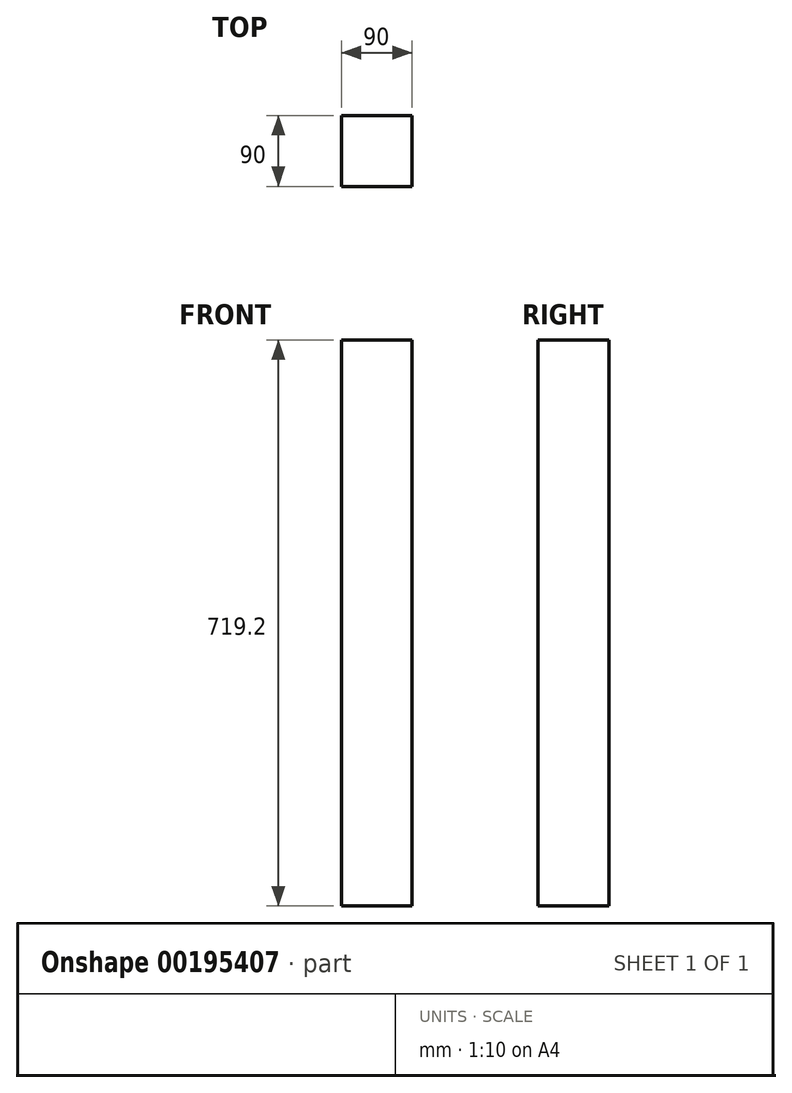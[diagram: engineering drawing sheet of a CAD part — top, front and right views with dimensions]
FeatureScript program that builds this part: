
annotation { "Feature Type Name" : "Feature", "Feature Type Description" : "" }
export const myFeature = defineFeature(function(context is Context, id is Id, definition is map)
    precondition{}
    {
        {
            var Q0;
            Q0=qCreatedBy(makeId("Top.planeOp"),FACE);
            var sketch = newSketch(context, id + "F0", { "sketchPlane" : qUnion([Q0])});
            skLineSegment(sketch, "E0.bottom", {"start": v(45, -45) * mm, "end": v(-45, -45) * mm});
            skLineSegment(sketch, "E0.top", {"start": v(45, 45) * mm, "end": v(-45, 45) * mm});
            skLineSegment(sketch, "E0.left", {"start": v(45, -45) * mm, "end": v(45, 45) * mm});
            skLineSegment(sketch, "E0.right", {"start": v(-45, -45) * mm, "end": v(-45, 45) * mm});
            skPoint(sketch, "E0.middle", {"position": v(0, 0) * mm});
            skSolve(sketch);
        }
        {
            var Q0;
            Q0=makeQuery(id+"F0.imprint","IMPRINT",FACE,{"disambiguationData":[TD([[makeQuery(id+"F0.imprint","IMPRINT",EDGE,{"derivedFrom":sQuery(id+"F0.wireOp",EDGE,"E0.bottom")}),-1.0]])]});
            extrude(context, id + "F1", {"entities" : qUnion([Q0]), "depth" : (770 - 50.8) * mm});
        }
    });
